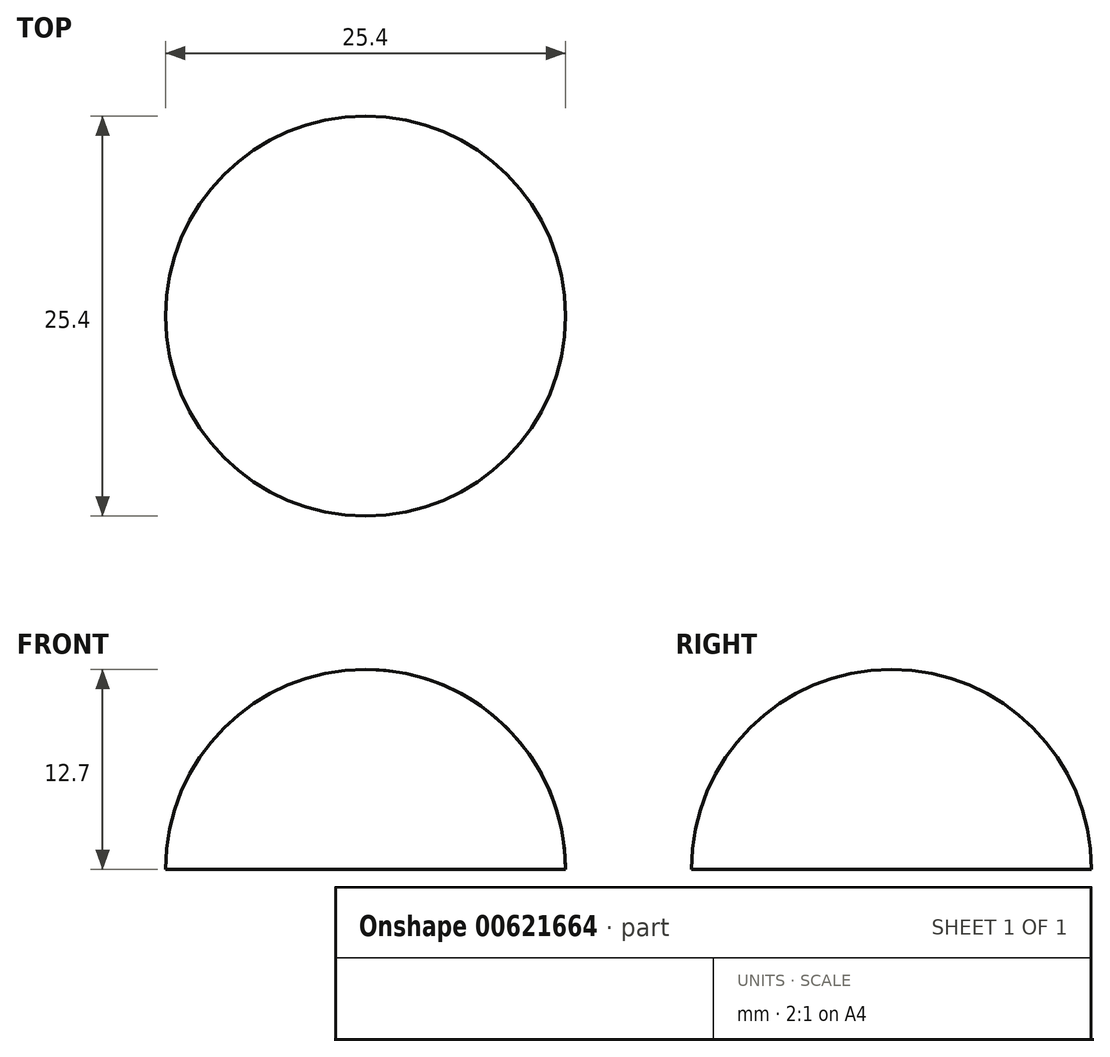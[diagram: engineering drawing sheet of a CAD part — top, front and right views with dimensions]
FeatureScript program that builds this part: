
annotation { "Feature Type Name" : "Feature", "Feature Type Description" : "" }
export const myFeature = defineFeature(function(context is Context, id is Id, definition is map)
    precondition{}
    {
        {
            var Q0;
            Q0=qCreatedBy(makeId("Front.planeOp"),FACE);
            var sketch = newSketch(context, id + "F0", { "sketchPlane" : qUnion([Q0])});
            skArc(sketch, "E0", {"start": v(0, 12.7) * mm, "mid": v(-8.98, 8.98) * mm, "end": v(-12.7, 0) * mm});
            skLineSegment(sketch, "E1", {"start": v(0, 30.14) * mm, "end": v(0, -25.35) * mm});
            skLineSegment(sketch, "E2", {"start": v(-27.19, 0) * mm, "end": v(36.73, 0) * mm});
            skArc(sketch, "E3.0", {"start": v(0, 11.7) * mm, "mid": v(-8.27, 8.27) * mm, "end": v(-11.7, 0) * mm});
            skSolve(sketch);
        }
        {
            var Q0;
            Q0 = qSketchRegion(id + "F0", true);
            var Q1;
            Q1=sQuery(id+"F0.wireOp",EDGE,"E1");
            revolve(context, id + "F1", {"surfaceOperationType" : NewSurfaceOperationType.NEW, "entities" : qUnion([Q0]), "axis" : qUnion([Q1]), "revolveType" : RevolveType.FULL});
        }
    });
